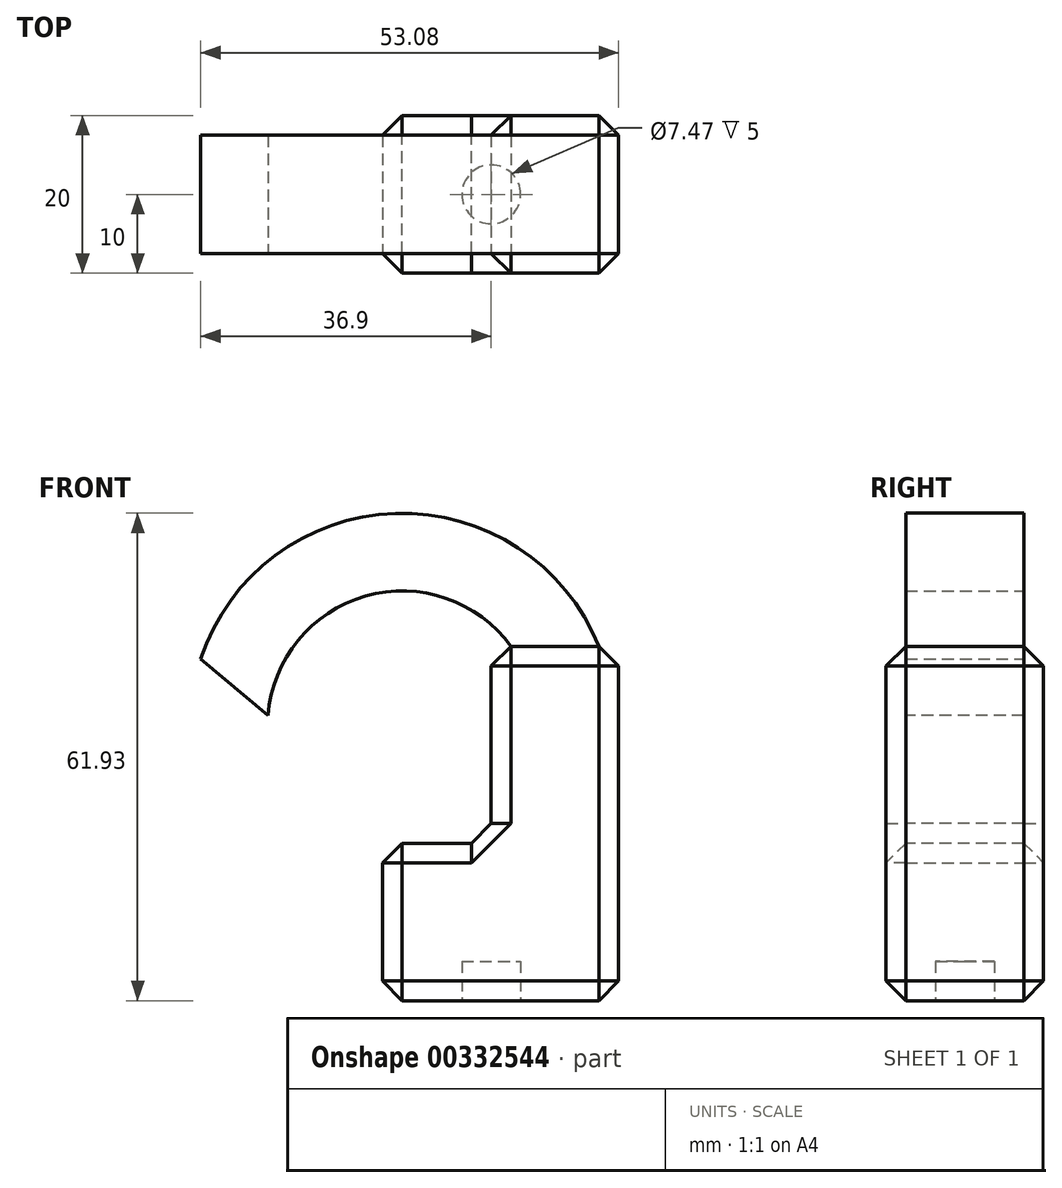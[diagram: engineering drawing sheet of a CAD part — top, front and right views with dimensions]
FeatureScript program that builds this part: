
annotation { "Feature Type Name" : "Feature", "Feature Type Description" : "" }
export const myFeature = defineFeature(function(context is Context, id is Id, definition is map)
    precondition{}
    {
        {
            var Q0;
            Q0=qCreatedBy(makeId("Top.planeOp"),FACE);
            var sketch = newSketch(context, id + "F0", { "sketchPlane" : qUnion([Q0])});
            skLineSegment(sketch, "E0.bottom", {"start": v(16.18, 10) * mm, "end": v(-13.82, 10) * mm});
            skLineSegment(sketch, "E0.top", {"start": v(16.18, -10) * mm, "end": v(-13.82, -10) * mm});
            skLineSegment(sketch, "E0.left", {"start": v(16.18, 10) * mm, "end": v(16.18, -10) * mm});
            skLineSegment(sketch, "E0.right", {"start": v(-13.82, 10) * mm, "end": v(-13.82, -10) * mm});
            skPoint(sketch, "E0.middle", {"position": v(1.18, 0) * mm});
            skSolve(sketch);
        }
        {
            var Q0;
            Q0=makeQuery(id+"F0.imprint","IMPRINT",FACE,{"disambiguationData":[TD([[makeQuery(id+"F0.imprint","IMPRINT",EDGE,{"derivedFrom":sQuery(id+"F0.wireOp",EDGE,"E0.bottom")}),1.0]])]});
            extrude(context, id + "F1", {"entities" : qUnion([Q0]), "depth" : 20 * mm});
        }
        {
            var Q0;
            Q0=makeQuery(id+"F1.opExtrude","CAP_FACE",FACE,{"disambiguationData":[OSD([sQuery(id+"F0.wireOp",EDGE,"E0.bottom"),sQuery(id+"F0.wireOp",EDGE,"E0.top"),sQuery(id+"F0.wireOp",EDGE,"E0.left"),sQuery(id+"F0.wireOp",EDGE,"E0.right")])],"isStart":false});
            var sketch = newSketch(context, id + "F2", { "sketchPlane" : qUnion([Q0])});
            skLineSegment(sketch, "E1.bottom", {"start": v(0, -10) * mm, "end": v(16.18, -10) * mm});
            skLineSegment(sketch, "E1.top", {"start": v(0, 10) * mm, "end": v(16.18, 10) * mm});
            skLineSegment(sketch, "E1.left", {"start": v(0, -10) * mm, "end": v(0, 10) * mm});
            skLineSegment(sketch, "E1.right", {"start": v(16.18, -10) * mm, "end": v(16.18, 10) * mm});
            skSolve(sketch);
        }
        {
            var Q0;
            Q0=makeQuery(id+"F2.imprint","IMPRINT",FACE,{"disambiguationData":[TD([[makeQuery(id+"F2.imprint","IMPRINT",EDGE,{"derivedFrom":sQuery(id+"F2.wireOp",EDGE,"E1.bottom")}),-1.0]])]});
            extrude(context, id + "F3", {"entities" : qUnion([Q0]), "operationType" : NewBodyOperationType.ADD, "depth" : 25 * mm});
        }
        {
            var Q0;
            Q0=makeQuery(id+"F3.boolean.opBoolean","MERGE",FACE,{"derivedFrom":[makeQuery(id+"F1.opExtrude","SWEPT_FACE",FACE,{"disambiguationData":[OSD([sQuery(id+"F0.wireOp",EDGE,"E0.top")])]}),makeQuery(id+"F3.opExtrude","SWEPT_FACE",FACE,{"disambiguationData":[OSD([sQuery(id+"F2.wireOp",EDGE,"E1.bottom")])]})]});
            var Q1;
            Q1=makeQuery(id+"F3.boolean.opBoolean","MERGE",FACE,{"derivedFrom":[makeQuery(id+"F1.opExtrude","SWEPT_FACE",FACE,{"disambiguationData":[OSD([sQuery(id+"F0.wireOp",EDGE,"E0.left")])]}),makeQuery(id+"F3.opExtrude","SWEPT_FACE",FACE,{"disambiguationData":[OSD([sQuery(id+"F2.wireOp",EDGE,"E1.right")])]})]});
            var Q2;
            Q2=makeQuery(id+"F1.opExtrude","CAP_FACE",FACE,{"disambiguationData":[OSD([sQuery(id+"F0.wireOp",EDGE,"E0.bottom"),sQuery(id+"F0.wireOp",EDGE,"E0.top"),sQuery(id+"F0.wireOp",EDGE,"E0.left"),sQuery(id+"F0.wireOp",EDGE,"E0.right")])],"isStart":false});
            var Q3;
            Q3=makeQuery(id+"F3.opExtrude","CAP_FACE",FACE,{"disambiguationData":[OSD([sQuery(id+"F2.wireOp",EDGE,"E1.bottom"),sQuery(id+"F2.wireOp",EDGE,"E1.top"),sQuery(id+"F2.wireOp",EDGE,"E1.left"),sQuery(id+"F2.wireOp",EDGE,"E1.right")])],"isStart":false});
            var Q4;
            Q4=makeQuery(id+"F3.boolean.opBoolean","MERGE",FACE,{"derivedFrom":[makeQuery(id+"F1.opExtrude","SWEPT_FACE",FACE,{"disambiguationData":[OSD([sQuery(id+"F0.wireOp",EDGE,"E0.bottom")])]}),makeQuery(id+"F3.opExtrude","SWEPT_FACE",FACE,{"disambiguationData":[OSD([sQuery(id+"F2.wireOp",EDGE,"E1.top")])]})]});
            var Q5;
            Q5=makeQuery(id+"F1.opExtrude","SWEPT_FACE",FACE,{"disambiguationData":[OSD([sQuery(id+"F0.wireOp",EDGE,"E0.right")])]});
            chamfer(context, id + "F4", {"entities" : qUnion([Q0, Q1, Q2, Q3, Q4, Q5]), "width" : 2.5 * mm, "tangentPropagation" : true});
        }
        {
            var Q0;
            Q0=makeQuery(id+"F1.opExtrude","CAP_FACE",FACE,{"disambiguationData":[OSD([sQuery(id+"F0.wireOp",EDGE,"E0.bottom"),sQuery(id+"F0.wireOp",EDGE,"E0.top"),sQuery(id+"F0.wireOp",EDGE,"E0.left"),sQuery(id+"F0.wireOp",EDGE,"E0.right")])],"isStart":true});
            var sketch = newSketch(context, id + "F5", { "sketchPlane" : qUnion([Q0])});
            skCircle(sketch, "E2", {"center": v(0, 0) * mm, "radius": 3.73 * mm});
            skSolve(sketch);
        }
        {
            var Q0;
            Q0=makeQuery(id+"F5.imprint","IMPRINT",FACE,{"disambiguationData":[TD([[makeQuery(id+"F5.imprint","IMPRINT",EDGE,{"derivedFrom":sQuery(id+"F5.wireOp",EDGE,"E2")}),1.0]])]});
            extrude(context, id + "F6", {"entities" : qUnion([Q0]), "operationType" : NewBodyOperationType.REMOVE, "oppositeDirection" : true, "depth" : 5 * mm});
        }
        {
            var Q0;
            Q0=makeQuery(id+"F1.opExtrude","CAP_FACE",FACE,{"disambiguationData":[OSD([sQuery(id+"F0.wireOp",EDGE,"E0.bottom"),sQuery(id+"F0.wireOp",EDGE,"E0.top"),sQuery(id+"F0.wireOp",EDGE,"E0.left"),sQuery(id+"F0.wireOp",EDGE,"E0.right")])],"isStart":false});
            extrude(context, id + "F7", {"entities" : qUnion([Q0]), "operationType" : NewBodyOperationType.ADD, "depth" : 15 * mm});
        }
        {
            var Q0;
            Q0=makeQuery(id+"F3.opExtrude","CAP_FACE",FACE,{"disambiguationData":[OSD([sQuery(id+"F2.wireOp",EDGE,"E1.bottom"),sQuery(id+"F2.wireOp",EDGE,"E1.top"),sQuery(id+"F2.wireOp",EDGE,"E1.left"),sQuery(id+"F2.wireOp",EDGE,"E1.right")])],"isStart":false});
            var Q1;
            {var subQ0=sQuery(id+"F0.wireOp",EDGE,"E0.right");var subQ1=sQuery(id+"F0.wireOp",EDGE,"E0.left");var subQ2=sQuery(id+"F0.wireOp",EDGE,"E0.top");var subQ3=sQuery(id+"F0.wireOp",EDGE,"E0.bottom");Q1=makeQuery(id+"F7.opExtrude","CAP_EDGE",EDGE,{"disambiguationData":[OSD([subQ3,subQ2,subQ1,subQ0]),TDD([makeQuery(id+"F4.opChamfer","BLEND_EDGE",EDGE,{"blendedFrom":[makeQuery(id+"F1.opExtrude","CAP_EDGE",EDGE,{"disambiguationData":[OSD([subQ0])],"isStart":false}),makeQuery(id+"F1.opExtrude","CAP_FACE",FACE,{"disambiguationData":[OSD([subQ3,subQ2,subQ1,subQ0])],"isStart":false})],"blendedInto":[makeQuery(id+"F1.opExtrude","CAP_FACE",FACE,{"disambiguationData":[OSD([subQ3,subQ2,subQ1,subQ0])],"isStart":false})]})])],"isStart":false});}
            revolve(context, id + "F8", {"operationType" : NewBodyOperationType.ADD, "entities" : qUnion([Q0]), "axis" : qUnion([Q1]), "revolveType" : RevolveType.ONE_DIRECTION, "angle" : 140 * degree});
        }
        {
            var Q0;
            Q0=makeQuery(id+"F7.opExtrude","CAP_FACE",FACE,{"disambiguationData":[OSD([sQuery(id+"F0.wireOp",EDGE,"E0.bottom"),sQuery(id+"F0.wireOp",EDGE,"E0.top"),sQuery(id+"F0.wireOp",EDGE,"E0.left"),sQuery(id+"F0.wireOp",EDGE,"E0.right")])],"isStart":false});
            extrude(context, id + "F9", {"entities" : qUnion([Q0]), "operationType" : NewBodyOperationType.REMOVE, "oppositeDirection" : true, "depth" : 15 * mm});
        }
    });
